# Revit family: HC_Control Unit_F_MEPcontent_Itho Daalderop_Amber_Control Module_NL-NL
name_source: partatom
category: Mechanical Equipment
units: mm (PartAtom-declared; Revit-internal decimal feet)

## family parameters
Classification = None
Cut with Voids When Loaded = No
Host = Face
OmniClass Number = 23.75.65.11.11
OmniClass Title = Heating Controllers
Part Type = Normal
Room Calculation Point = No
Round Connector Dimension = Use Diameter
Shared = No

## types (1)
- Control Module
    Article Description = Amber regelmodule
    Article Type = Control Module
    Base Family Version = 23.10
    Black = Color RGB 040-040-040
    Content Supplier URL = www.MEPcontent.com
    Custom = No
    Dark Gray = Color RGB 050-050-050
    Default Elevation = 0 mm  [stored 0 ft]
    Depth = 136 mm
    Description = Amber regelmodule
    EMCS Version = 5.0
    ETIM Article Class = EC010927
    Family Version = 23.10
    GLN = 8712922000014
    Gray = Color RAL 7040
    Height = 450 mm  [stored 1.47638 ft]
    IFCExportAs = IfcController
    IFCExportType = NOTDEFINED
    MEPcontent Class = CONTROL_UNIT_HC
    Manufacturer = Itho Daalderop
    Manufacturer URL = https://www.ithodaalderop.nl
    Model = Control Module
    Product Line = Itho Daalderop
    Revit Version = 2021
    URL = https://mep.trimble.com
    White = Color RGB 230-230-230
    Width = 380 mm

note: [stored X ft] marks values corroborated as IEEE doubles in the binary element streams (Revit-internal decimal feet)

## geometry (parser evidence)
native form markers: Sweep x2
no freeform markers — native parametric forms only
